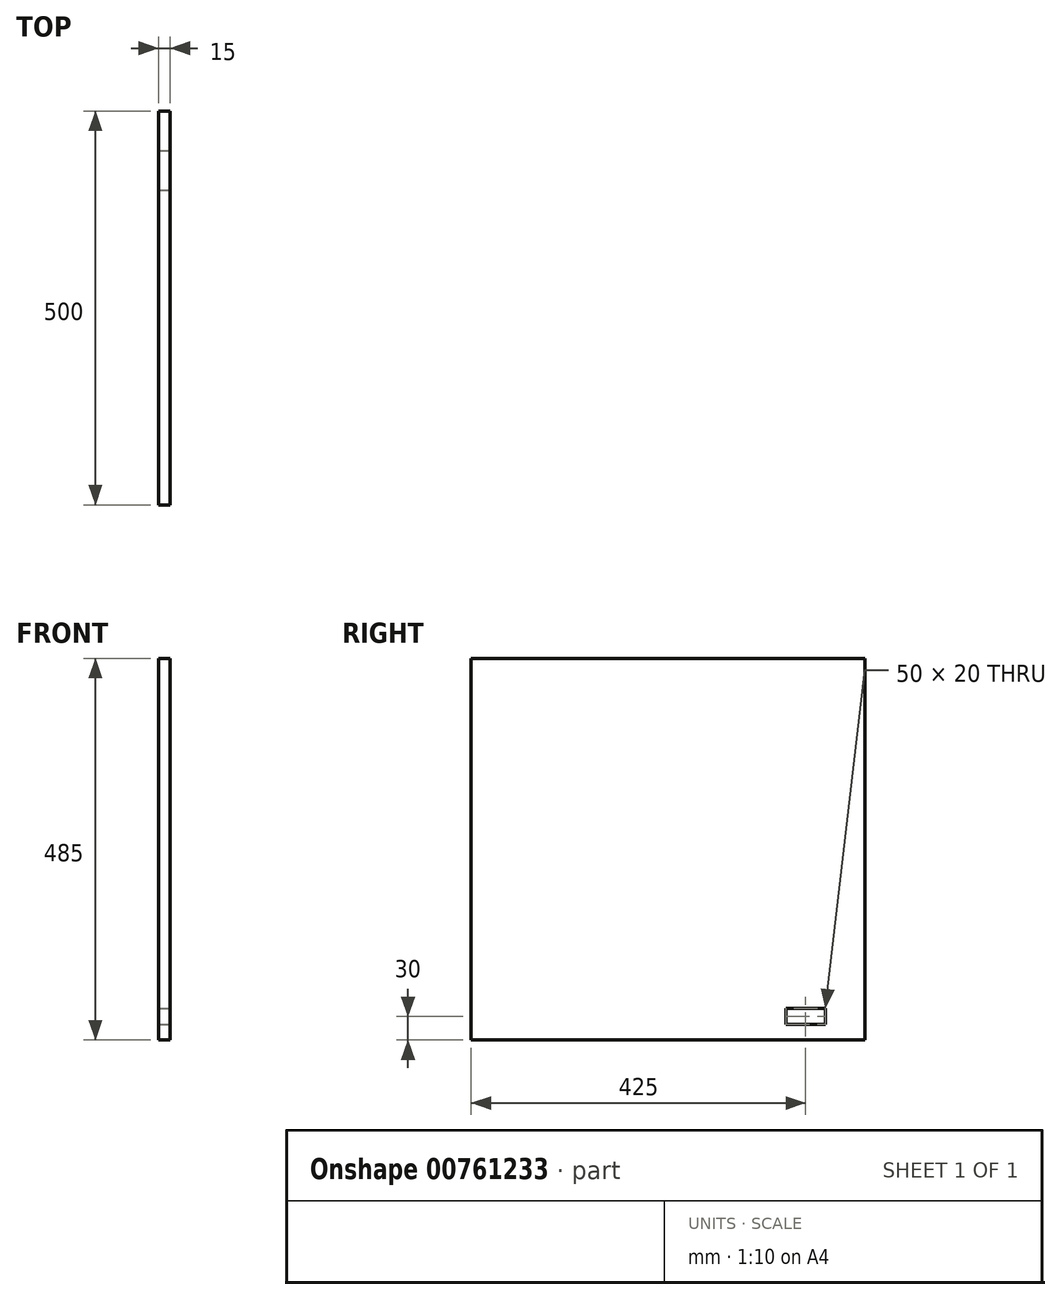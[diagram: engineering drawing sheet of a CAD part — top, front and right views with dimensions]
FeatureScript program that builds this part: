
annotation { "Feature Type Name" : "Feature", "Feature Type Description" : "" }
export const myFeature = defineFeature(function(context is Context, id is Id, definition is map)
    precondition{}
    {
        {
            var Q0;
            Q0=qCreatedBy(makeId("Right.planeOp"),FACE);
            var sketch = newSketch(context, id + "F0", { "sketchPlane" : qUnion([Q0])});
            skLineSegment(sketch, "E0.bottom", {"start": v(250, -242.5) * mm, "end": v(-250, -242.5) * mm});
            skLineSegment(sketch, "E0.top", {"start": v(250, 242.5) * mm, "end": v(-250, 242.5) * mm});
            skLineSegment(sketch, "E0.left", {"start": v(250, -242.5) * mm, "end": v(250, 242.5) * mm});
            skLineSegment(sketch, "E0.right", {"start": v(-250, -242.5) * mm, "end": v(-250, 242.5) * mm});
            skPoint(sketch, "E0.middle", {"position": v(0, 0) * mm});
            skSolve(sketch);
        }
        {
            var Q0;
            Q0=makeQuery(id+"F0.imprint","IMPRINT",FACE,{"disambiguationData":[TD([[makeQuery(id+"F0.imprint","IMPRINT",EDGE,{"derivedFrom":sQuery(id+"F0.wireOp",EDGE,"E0.bottom")}),-1.0]])]});
            extrude(context, id + "F1", {"entities" : qUnion([Q0]), "depth" : 15 * mm, "offsetDistance" : 25 * mm});
        }
        {
            var Q0;
            Q0=makeQuery(id+"F1.opExtrude","CAP_FACE",FACE,{"disambiguationData":[OSD([sQuery(id+"F0.wireOp",EDGE,"E0.bottom"),sQuery(id+"F0.wireOp",EDGE,"E0.top"),sQuery(id+"F0.wireOp",EDGE,"E0.left"),sQuery(id+"F0.wireOp",EDGE,"E0.right")])],"isStart":false});
            var sketch = newSketch(context, id + "F2", { "sketchPlane" : qUnion([Q0])});
            skLineSegment(sketch, "E1.bottom", {"start": v(200, -202.5) * mm, "end": v(150, -202.5) * mm});
            skLineSegment(sketch, "E1.top", {"start": v(200, -222.5) * mm, "end": v(150, -222.5) * mm});
            skLineSegment(sketch, "E1.left", {"start": v(200, -202.5) * mm, "end": v(200, -222.5) * mm});
            skLineSegment(sketch, "E1.right", {"start": v(150, -202.5) * mm, "end": v(150, -222.5) * mm});
            skPoint(sketch, "E1.middle", {"position": v(175, -212.5) * mm});
            skSolve(sketch);
        }
        {
            var Q0;
            Q0=makeQuery(id+"F2.imprint","IMPRINT",FACE,{"disambiguationData":[TD([[makeQuery(id+"F2.imprint","IMPRINT",EDGE,{"derivedFrom":sQuery(id+"F2.wireOp",EDGE,"E1.bottom")}),1.0]])]});
            extrude(context, id + "F3", {"entities" : qUnion([Q0]), "operationType" : NewBodyOperationType.REMOVE, "endBound" : BoundingType.THROUGH_ALL, "oppositeDirection" : true, "depth" : 25 * mm, "offsetDistance" : 25 * mm});
        }
    });
